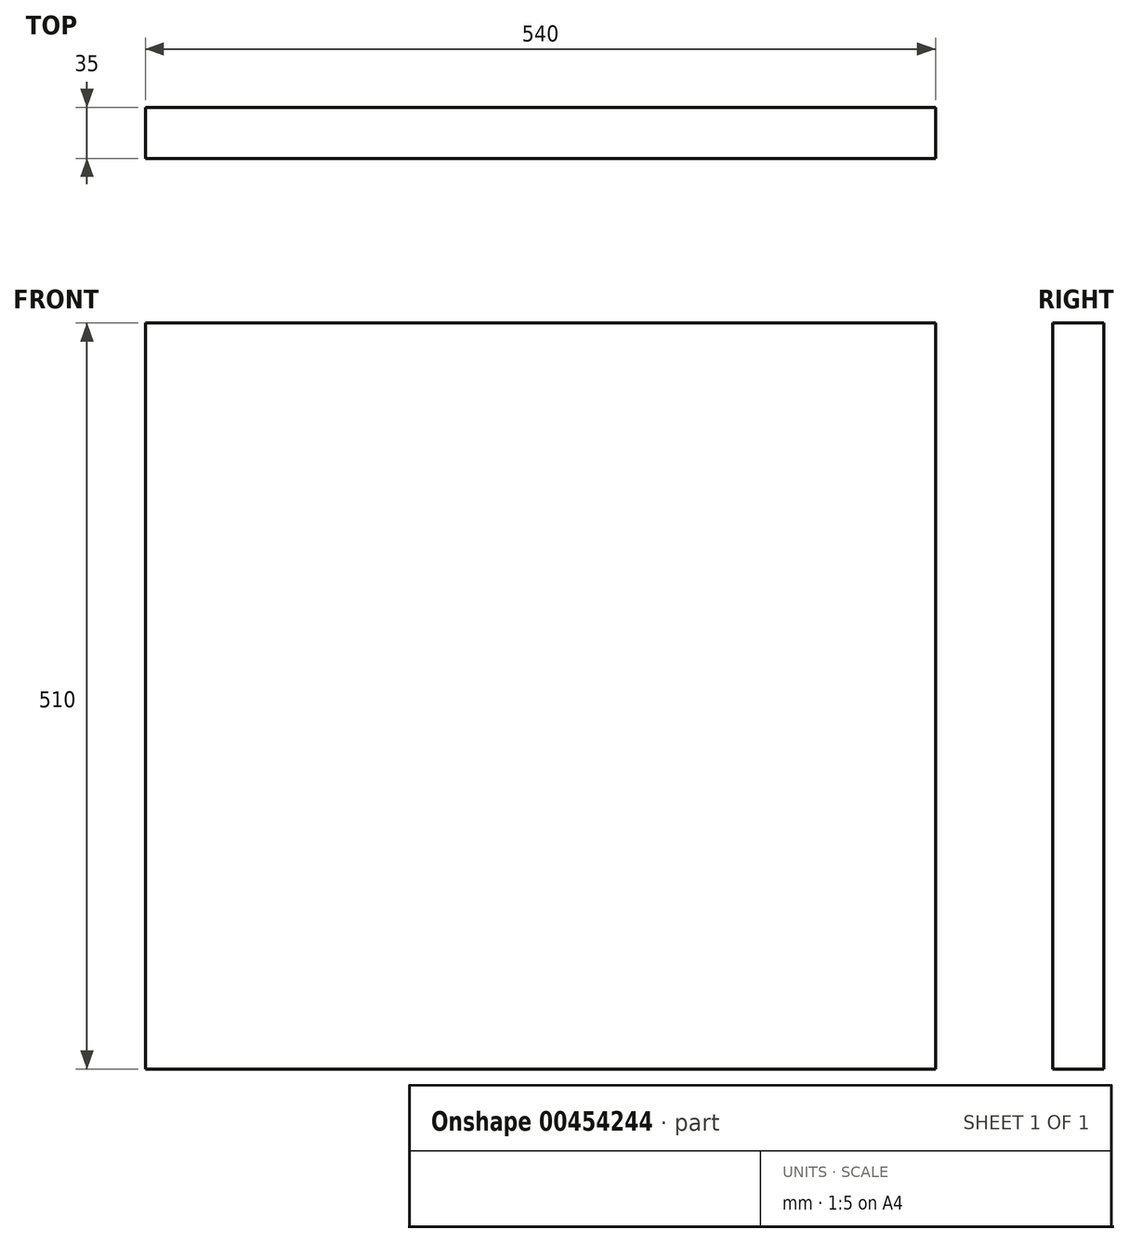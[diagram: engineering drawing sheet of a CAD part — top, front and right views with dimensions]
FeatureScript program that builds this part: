
annotation { "Feature Type Name" : "Feature", "Feature Type Description" : "" }
export const myFeature = defineFeature(function(context is Context, id is Id, definition is map)
    precondition{}
    {
        {
            var Q0;
            Q0=qCreatedBy(makeId("Front.planeOp"),FACE);
            var sketch = newSketch(context, id + "F0", { "sketchPlane" : qUnion([Q0])});
            skLineSegment(sketch, "E0.bottom", {"start": v(-270, 255) * mm, "end": v(270, 255) * mm});
            skLineSegment(sketch, "E0.top", {"start": v(-270, -255) * mm, "end": v(270, -255) * mm});
            skLineSegment(sketch, "E0.left", {"start": v(-270, 255) * mm, "end": v(-270, -255) * mm});
            skLineSegment(sketch, "E0.right", {"start": v(270, 255) * mm, "end": v(270, -255) * mm});
            skPoint(sketch, "E0.middle", {"position": v(0, 0) * mm});
            skSolve(sketch);
        }
        {
            var Q0;
            Q0 = qSketchRegion(id + "F0", true);
            extrude(context, id + "F1", {"entities" : qUnion([Q0]), "depth" : 35 * mm});
        }
    });
